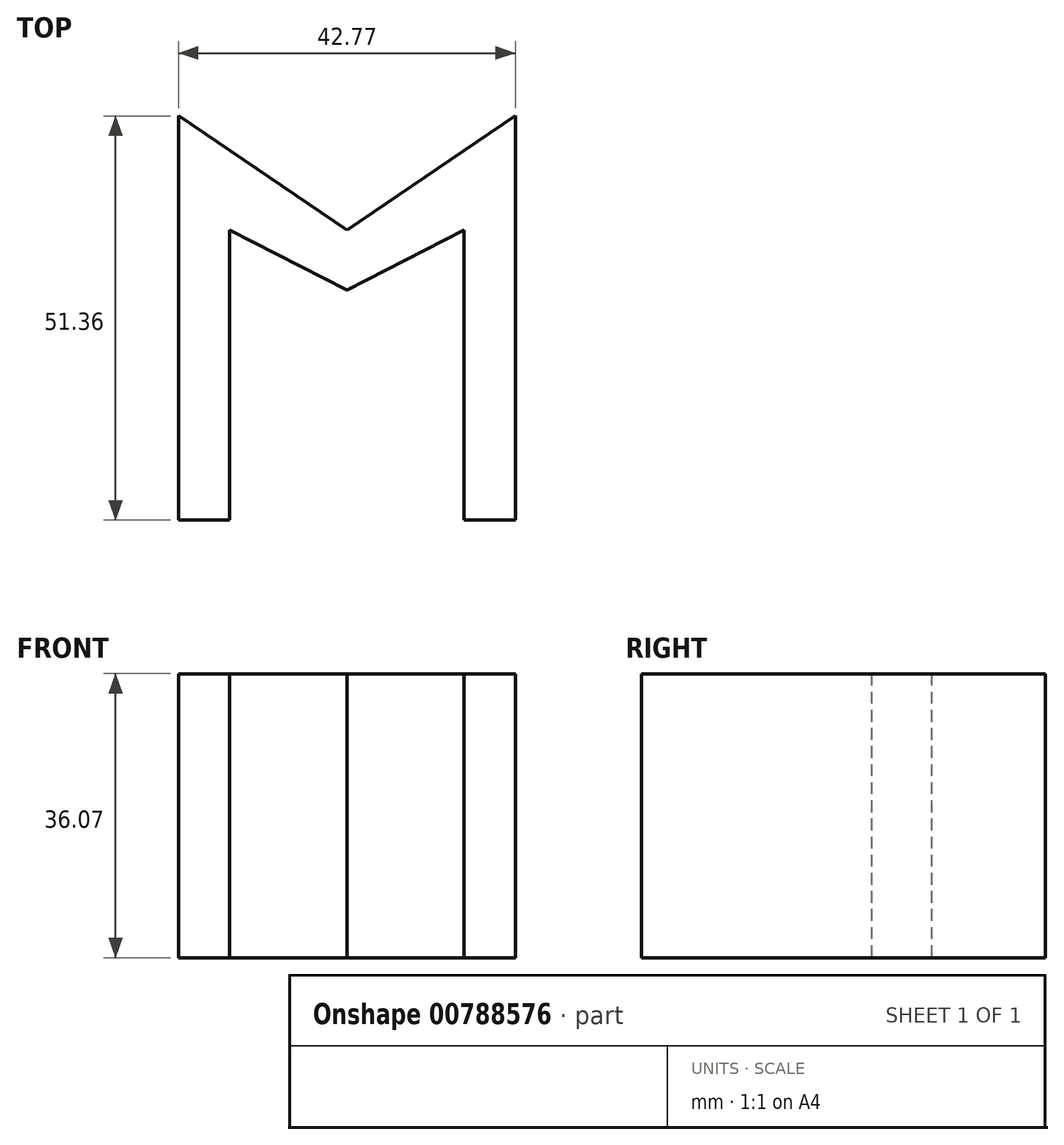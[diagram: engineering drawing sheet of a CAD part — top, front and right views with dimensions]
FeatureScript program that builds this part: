
annotation { "Feature Type Name" : "Feature", "Feature Type Description" : "" }
export const myFeature = defineFeature(function(context is Context, id is Id, definition is map)
    precondition{}
    {
        {
            var Q0;
            Q0=qCreatedBy(makeId("Top.planeOp"),FACE);
            var sketch = newSketch(context, id + "F0", { "sketchPlane" : qUnion([Q0])});
            skLineSegment(sketch, "E0", {"start": v(-39.81, -17.47) * mm, "end": v(-39.81, 33.9) * mm});
            skLineSegment(sketch, "E1", {"start": v(-39.81, 33.9) * mm, "end": v(-18.43, 19.38) * mm});
            skLineSegment(sketch, "E2", {"start": v(-18.43, 19.38) * mm, "end": v(2.96, 33.9) * mm});
            skLineSegment(sketch, "E3", {"start": v(2.96, 33.9) * mm, "end": v(2.96, -17.47) * mm});
            skLineSegment(sketch, "E4", {"start": v(2.96, -17.47) * mm, "end": v(-3.53, -17.47) * mm});
            skLineSegment(sketch, "E5", {"start": v(-3.53, -17.47) * mm, "end": v(-3.53, 19.38) * mm});
            skLineSegment(sketch, "E6", {"start": v(-3.53, 19.38) * mm, "end": v(-18.43, 11.74) * mm});
            skLineSegment(sketch, "E7", {"start": v(-18.43, 11.74) * mm, "end": v(-33.32, 19.38) * mm});
            skLineSegment(sketch, "E8", {"start": v(-33.32, 19.38) * mm, "end": v(-33.32, -17.47) * mm});
            skLineSegment(sketch, "E9", {"start": v(-39.81, -17.47) * mm, "end": v(-33.32, -17.47) * mm});
            skSolve(sketch);
        }
        {
            var Q0;
            Q0=makeQuery(id+"F0.imprint","IMPRINT",FACE,{"disambiguationData":[TD([[makeQuery(id+"F0.imprint","IMPRINT",EDGE,{"derivedFrom":sQuery(id+"F0.wireOp",EDGE,"E0")}),-1.0]])]});
            extrude(context, id + "F1", {"entities" : qUnion([Q0]), "depth" : 36.07 * mm, "offsetDistance" : 25.4 * mm});
        }
    });
